# Revit family: Hager-VEGA-Surface_mounted-IP40-With_Cover-With_DIN-Hosted-PL-pl
name_source: partatom
category: Electrical Equipment
units: mm (PartAtom-declared; Revit-internal decimal feet)

## family parameters
Cut with Voids When Loaded = No
Host = Face
Maintain Annotation Orientation = Yes
Panel Configuration = Two Columns, Circuits Across
Part Type = Panelboard
Room Calculation Point = No
Round Connector Dimension = Use Diameter
Shared = No

## types (11) — shared parameters
BC_MODEL_ID = 1547041
BC_OBJECT_ID = 513451
BC_OBJECT_VERSION = #5
Code hager = ADD-EC000214_EU
EF000003 - Sposób montażu = Montaż natynkowy
EF000007 - Kolor = Biały
EF000008 - Szerokość = 400 mm  [stored 1.31234 ft]
EF000024 - Odporność na promieniowanie UV = No
EF000049 - Głębokość = 146 mm  [stored 0.479003 ft]
EF000116 - Numer RAL = 9010
EF001062 - Wykonanie zgodne z Dyrektywą Kompatybilności Elektromagnetycznej EMC = No
EF001088 - Możliwość rozbudowy = Yes
EF001134 - Szyna DIN = Yes
EF002950 - Szerokość wyrażona liczbą modułów = 18
EF004462 - Rodzaj zamknięcia = Inne
EF005474 - Stopień ochrony (IP) = IP40
EF006306 - Z zamkiem = No
EF015776 - Listwa zaciskowa uziemienia = Yes
EF015941 - Drzwi przepuszczające sygnał = Yes
ETIM class code = EC000214
ETIM class name = Small distribution board
HG000002-with door or cover-pl = Yes
HG000003-Range-pl = VEGA
HG000005-Thickness-pl = 2 mm  [stored 0.00656168 ft]
HG000006-Flush mounted-pl = No
HG000009-Double swing door-pl = No
HG000010-Asymmetric doors-pl = No
HG000011-Empty rows from bottom-pl = No
HG000012-Door swing angle-pl = 90.00°
HG000013-Door on the left-pl = No
HG000014-Door on the right-pl = Yes
HG000015-Clearance visibility-pl = Yes
HG000016-Door 3D visibility-pl = Yes
HG000017-Distance between poles-pl = 18 mm  [stored 0.0590551 ft]
HG000060-RAL-number = 9010
HG000099-Onfly Template ID-pl-PL = 507532
HGEF0002950-Szerokość wyrażona liczbą modułów = 18
Manufacturer = Hager
Name = VEGA-Surface_mounted-IP40-With_Cover-With_DIN-PL
Name BIM&CO = Electricity
Name hager = ADD_Enclosures_EC000214
Uniformat = Low Tension Service & Dist.
Uniformat code = D501001
zero-valued in all types: Default Elevation, EF000218 - Głębokość wbudowania, EF000332 - Wysokość wbudowania, EF000846 - Szerokość wbudowania, EF001131 - Głębokość wewnętrzna, HG000007-Number of empty columns-pl, HG000008-Number of empty rows-pl

## per-type parameters (varying)
| type | BC_VARIANT_ID | EF000040 - Wysokość | EF000118 - Z płytą montażową | EF000266 - Liczba rzędów | EF006244 - Transparentna pokrywa/drzwi | EF009212 - Wykonanie/rodzaj pokrywy | EF015777 - Listwa zaciskowa przewodu neutralnego | HG000001-Number of columns-pl | HG000004-Manufacturer reference-pl | HGEF000266-Liczba rzędów |
| VEGA-Surface_mounted_W400_H325_D146_18_Modular_Spacing-VB118MP | 1174002 | 325 mm  [stored 1.06627 ft] | Yes | 0 | No | Z otworem | No | 0 | VB118MP | 0 |
| VEGA-Surface_mounted_W400_H325_D146_18_Modular_Spacing-VB118PB | 1174003 | 325 mm  [stored 1.06627 ft] | No | 1 | No | Zamknięty | Yes | 1 | VB118PB | 1 |
| VEGA-Surface_mounted_W400_H325_D146_18_Modular_Spacing-VB118TB | 1174004 | 325 mm  [stored 1.06627 ft] | No | 1 | Yes | Zamknięty | Yes | 1 | VB118TB | 1 |
| VEGA-Surface_mounted_W400_H475_D146_18_Modular_Spacing-VB218MP | 1174005 | 475 mm  [stored 1.5584 ft] | Yes | 0 | No | Z otworem | No | 0 | VB218MP | 0 |
| VEGA-Surface_mounted_W400_H475_D146_18_Modular_Spacing-VB218PB | 1174006 | 475 mm  [stored 1.5584 ft] | No | 2 | No | Zamknięty | Yes | 1 | VB218PB | 2 |
| VEGA-Surface_mounted_W400_H475_D146_18_Modular_Spacing-VB218TB | 1174007 | 475 mm  [stored 1.5584 ft] | No | 2 | Yes | Zamknięty | Yes | 1 | VB218TB | 2 |
| VEGA-Surface_mounted_W400_H625_D146_18_Modular_Spacing-VB318MP | 1174008 | 625 mm  [stored 2.05052 ft] | Yes | 0 | No | Z otworem | No | 0 | VB318MP | 0 |
| VEGA-Surface_mounted_W400_H625_D146_18_Modular_Spacing-VB318PB | 1174009 | 625 mm  [stored 2.05052 ft] | No | 3 | No | Zamknięty | Yes | 1 | VB318PB | 3 |
| VEGA-Surface_mounted_W400_H625_D146_18_Modular_Spacing-VB318TB | 1174010 | 625 mm  [stored 2.05052 ft] | No | 3 | Yes | Zamknięty | Yes | 1 | VB318TB | 3 |
| VEGA-Surface_mounted_W400_H775_D146_18_Modular_Spacing-VB418PB | 1174011 | 775 mm  [stored 2.54265 ft] | No | 4 | No | Zamknięty | Yes | 1 | VB418PB | 4 |
| VEGA-Surface_mounted_W400_H775_D146_18_Modular_Spacing-VB418TB | 1174012 | 775 mm  [stored 2.54265 ft] | No | 4 | Yes | Zamknięty | Yes | 1 | VB418TB | 4 |

note: column(s) folded — value = type name in every type: Reference

note: [stored X ft] marks values corroborated as IEEE doubles in the binary element streams (Revit-internal decimal feet)

## geometry (parser evidence)
native form markers: Sweep x14
no freeform markers — native parametric forms only
